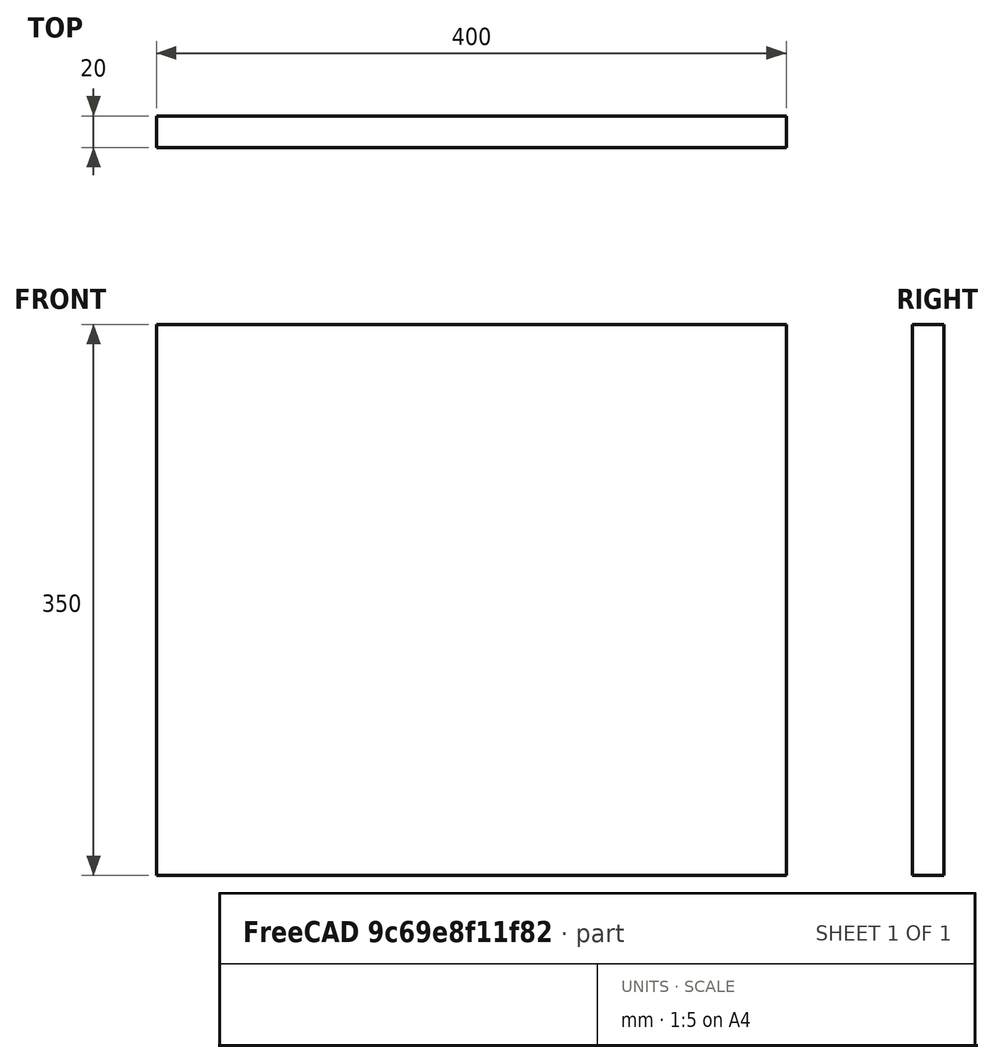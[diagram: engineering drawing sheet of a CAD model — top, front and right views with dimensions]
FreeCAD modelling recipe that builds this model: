
FCSTD DOCUMENT  (FreeCAD 0.16R6706 (Git))
Label: base_plate
License: All rights reserved
LicenseURL: http://en.wikipedia.org/wiki/All_rights_reserved
objects: Sketcher::SketchObject×1, PartDesign::Pad×1, Part::Feature×1
note: 4 computed .brp shape members not serialized (recipe doc carries the construction recipe); baked Part::Feature solids carry a one-line shape summary decoded from their .brp

FEATURE [Sketcher::SketchObject] Sketch
  Placement = pos=(0,0,0) rot=(1,0,0;1.5708rad)
  sketch-geometry (4):
    g0: LineSegment StartX=0 StartY=0 StartZ=0 EndX=400 EndY=0 EndZ=0
    g1: LineSegment StartX=400 StartY=0 StartZ=0 EndX=400 EndY=350 EndZ=0
    g2: LineSegment StartX=400 StartY=350 StartZ=0 EndX=0 EndY=350 EndZ=0
    g3: LineSegment StartX=0 StartY=350 StartZ=0 EndX=0 EndY=0 EndZ=0
  constraints (11):
    c: Coincident(g0,g1)
    c: Coincident(g1,g2)
    c: Coincident(g2,g3)
    c: Coincident(g3,g0)
    c: Horizontal(g0)
    c: Horizontal(g2)
    c: Vertical(g1)
    c: Vertical(g3)
    c: Coincident(g0,g-1)
    c: DistanceX(g0,g0) = 400
    c: DistanceY(g3,g3) = 350
FEATURE [PartDesign::Pad] Pad
  Length = 20
  Length2 = 100
  Placement = pos=(0,0,0) rot=(1,0,0;1.5708rad)
  Sketch = -> Sketch
  Type = 0
FEATURE [Part::Feature] Pad001
  Placement = pos=(0,0,0) rot=(1,0,0;1.5708rad)
  shape: bbox 400 x 20 x 350 mm, 6 faces (baked)
